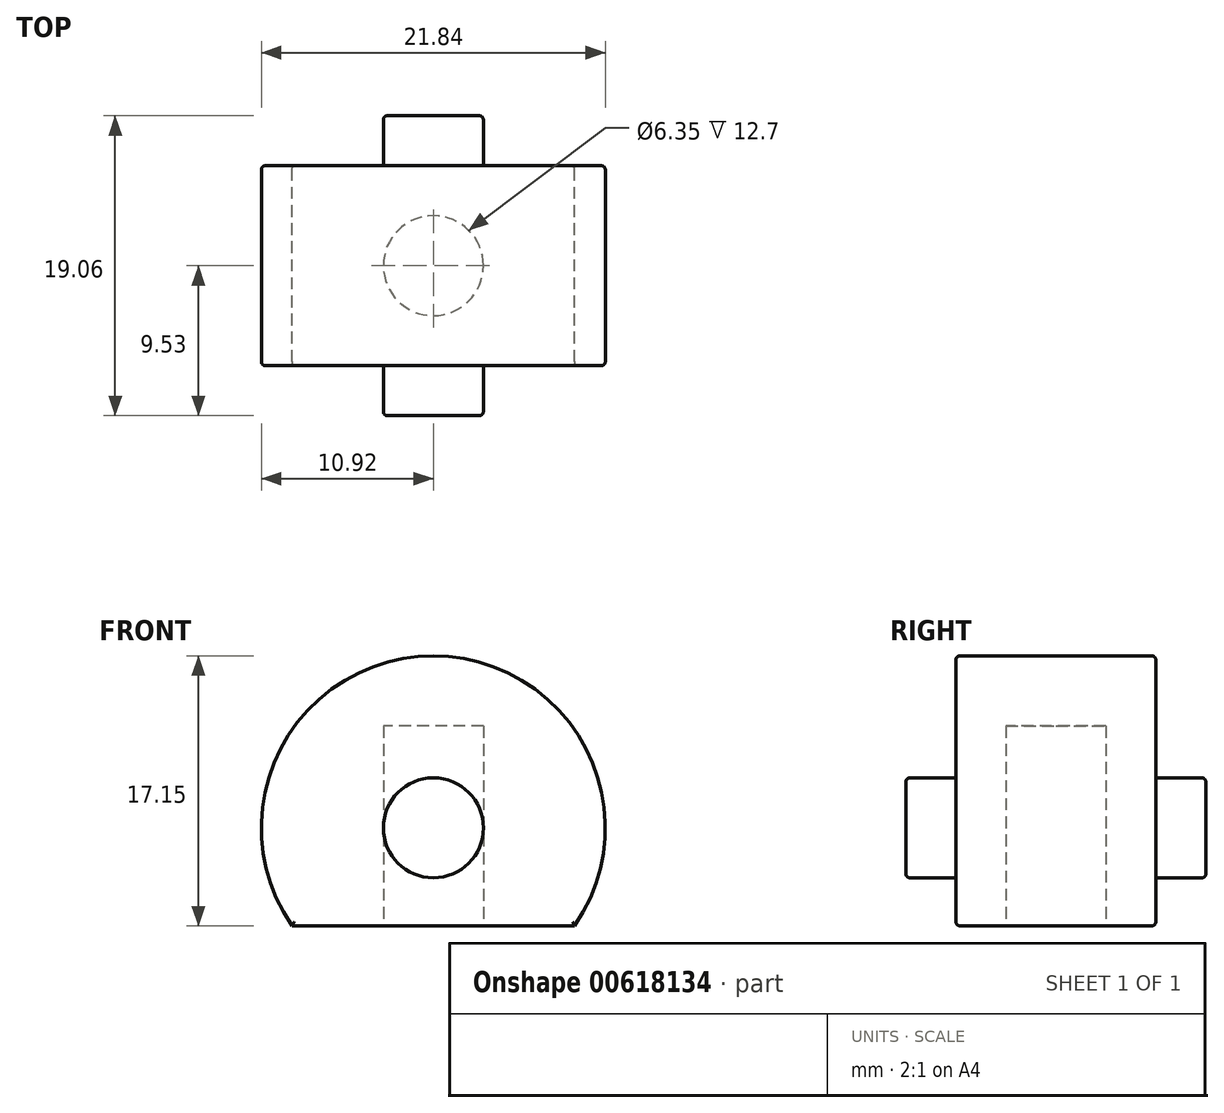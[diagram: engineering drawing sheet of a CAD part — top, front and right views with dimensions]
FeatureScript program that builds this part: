
annotation { "Feature Type Name" : "Feature", "Feature Type Description" : "" }
export const myFeature = defineFeature(function(context is Context, id is Id, definition is map)
    precondition{}
    {
        {
            var Q0;
            Q0=qCreatedBy(makeId("Front.planeOp"),FACE);
            var sketch = newSketch(context, id + "F0", { "sketchPlane" : qUnion([Q0])});
            skArc(sketch, "E0", {"start": v(8.98, 0) * mm, "mid": v(0, 17.14) * mm, "end": v(-8.98, 0) * mm});
            skLineSegment(sketch, "E1", {"start": v(-8.98, 0) * mm, "end": v(8.98, 0) * mm});
            skSolve(sketch);
        }
        {
            var Q0;
            Q0=qCreatedBy(makeId("Front.planeOp"),FACE);
            var sketch = newSketch(context, id + "F1", { "sketchPlane" : qUnion([Q0])});
            skCircle(sketch, "E2", {"center": v(0, 6.22) * mm, "radius": 3.18 * mm});
            skSolve(sketch);
        }
        {
            var Q0;
            Q0=qCreatedBy(makeId("Top.planeOp"),FACE);
            var sketch = newSketch(context, id + "F2", { "sketchPlane" : qUnion([Q0])});
            skCircle(sketch, "E3", {"center": v(0, 0) * mm, "radius": 3.18 * mm});
            skSolve(sketch);
        }
        {
            var Q0;
            Q0 = qSketchRegion(id + "F0", true);
            extrude(context, id + "F3", {"entities" : qUnion([Q0]), "endBound" : BoundingType.SYMMETRIC, "depth" : 12.7 * mm, "offsetDistance" : 25.4 * mm});
        }
        {
            var Q0;
            Q0 = qSketchRegion(id + "F1", true);
            extrude(context, id + "F4", {"entities" : qUnion([Q0]), "operationType" : NewBodyOperationType.ADD, "endBound" : BoundingType.SYMMETRIC, "depth" : 19.05 * mm, "offsetDistance" : 25.4 * mm});
        }
        {
            var Q0;
            Q0 = qSketchRegion(id + "F2", true);
            extrude(context, id + "F5", {"entities" : qUnion([Q0]), "operationType" : NewBodyOperationType.REMOVE, "depth" : 12.7 * mm, "offsetDistance" : 25.4 * mm});
        }
        {
            var Q0;
            Q0=makeQuery(id+"F4.opExtrude","CAP_EDGE",EDGE,{"disambiguationData":[OSD([sQuery(id+"F1.wireOp",EDGE,"E2")])],"isStart":false});
            var Q1;
            Q1=makeQuery(id+"F3.opExtrude","CAP_EDGE",EDGE,{"disambiguationData":[OSD([sQuery(id+"F0.wireOp",EDGE,"E0")])],"isStart":false});
            var Q2;
            Q2=makeQuery(id+"F3.opExtrude","CAP_EDGE",EDGE,{"disambiguationData":[OSD([sQuery(id+"F0.wireOp",EDGE,"E0")])],"isStart":true});
            var Q3;
            Q3=makeQuery(id+"F4.opExtrude","CAP_EDGE",EDGE,{"disambiguationData":[OSD([sQuery(id+"F1.wireOp",EDGE,"E2")])],"isStart":true});
            var Q4;
            Q4=makeQuery(id+"F3.opExtrude","CAP_EDGE",EDGE,{"disambiguationData":[OSD([sQuery(id+"F0.wireOp",EDGE,"E1")])],"isStart":true});
            var Q5;
            Q5=makeQuery(id+"F3.opExtrude","CAP_EDGE",EDGE,{"disambiguationData":[OSD([sQuery(id+"F0.wireOp",EDGE,"E1")])],"isStart":false});
            fillet(context, id + "F6", {"entities" : qUnion([Q0, Q1, Q2, Q3, Q4, Q5]), "radius" : 0.25 * mm, "allowEdgeOverflow" : false});
        }
    });
